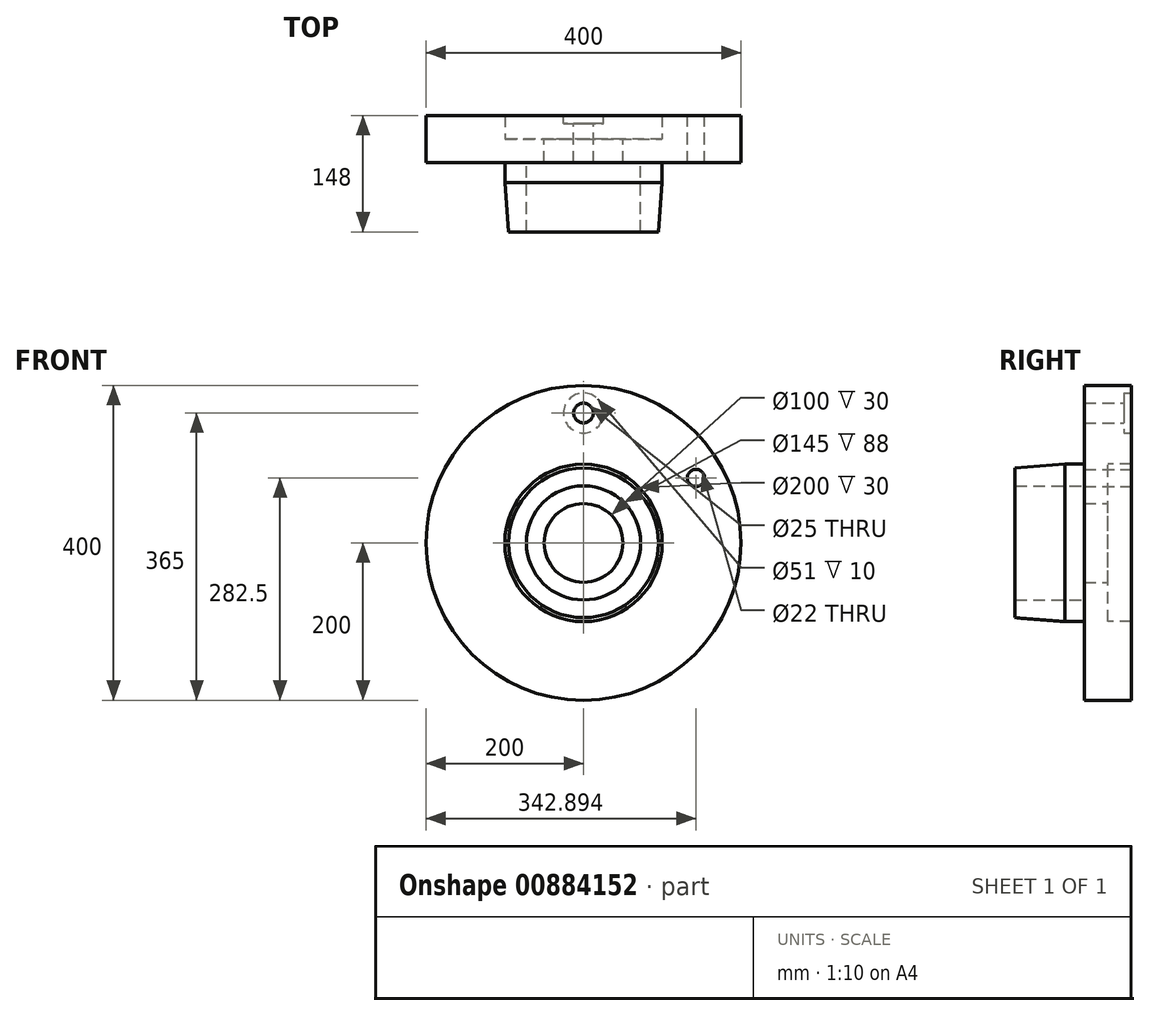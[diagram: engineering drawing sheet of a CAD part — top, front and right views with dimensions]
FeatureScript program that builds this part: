
annotation { "Feature Type Name" : "Feature", "Feature Type Description" : "" }
export const myFeature = defineFeature(function(context is Context, id is Id, definition is map)
    precondition{}
    {
        {
            var Q0;
            Q0=qCreatedBy(makeId("Front.planeOp"),FACE);
            var sketch = newSketch(context, id + "F0", { "sketchPlane" : qUnion([Q0])});
            skCircle(sketch, "E0", {"center": v(0, 0) * mm, "radius": 72.5 * mm});
            skCircle(sketch, "E1", {"center": v(0, 0) * mm, "radius": 100 * mm});
            skCircle(sketch, "E2", {"center": v(0, 0) * mm, "radius": 50 * mm});
            skCircle(sketch, "E3", {"center": v(0, 0) * mm, "radius": 200 * mm});
            skCircle(sketch, "E4", {"center": v(0, 0) * mm, "radius": 165 * mm, "construction": true});
            skPoint(sketch, "E5", {"position": v(0, 165) * mm});
            skLineSegment(sketch, "E6", {"start": v(0, 0) * mm, "end": v(142.9, 82.5) * mm, "construction": true});
            skPoint(sketch, "E7", {"position": v(142.9, 82.5) * mm});
            skSolve(sketch);
        }
        {
            var Q0;
            Q0=makeQuery(id+"F0.imprint","IMPRINT",FACE,{"disambiguationData":[TD([[makeQuery(id+"F0.imprint","IMPRINT",EDGE,{"derivedFrom":sQuery(id+"F0.wireOp",EDGE,"E0")}),-1.0]])]});
            var Q1;
            Q1=makeQuery(id+"F0.imprint","IMPRINT",FACE,{"disambiguationData":[TD([[makeQuery(id+"F0.imprint","IMPRINT",EDGE,{"derivedFrom":sQuery(id+"F0.wireOp",EDGE,"E0")}),1.0]])]});
            var Q2;
            Q2=makeQuery(id+"F0.imprint","IMPRINT",FACE,{"disambiguationData":[TD([[makeQuery(id+"F0.imprint","IMPRINT",EDGE,{"derivedFrom":sQuery(id+"F0.wireOp",EDGE,"E1")}),-1.0]])]});
            extrude(context, id + "F1", {"entities" : qUnion([Q0, Q1, Q2]), "depth" : 30 * mm, "offsetDistance" : 25 * mm});
        }
        {
            var Q0;
            Q0=makeQuery(id+"F0.imprint","IMPRINT",FACE,{"disambiguationData":[TD([[makeQuery(id+"F0.imprint","IMPRINT",EDGE,{"derivedFrom":sQuery(id+"F0.wireOp",EDGE,"E0")}),-1.0]])]});
            extrude(context, id + "F2", {"entities" : qUnion([Q0]), "operationType" : NewBodyOperationType.ADD, "depth" : (70 + 48) * mm, "offsetDistance" : 25 * mm});
        }
        {
            var Q0;
            Q0=makeQuery(id+"F0.imprint","IMPRINT",FACE,{"disambiguationData":[TD([[makeQuery(id+"F0.imprint","IMPRINT",EDGE,{"derivedFrom":sQuery(id+"F0.wireOp",EDGE,"E1")}),-1.0]])]});
            extrude(context, id + "F3", {"entities" : qUnion([Q0]), "operationType" : NewBodyOperationType.ADD, "oppositeDirection" : true, "depth" : 30 * mm, "offsetDistance" : 25 * mm});
        }
        {
            var Q0;
            Q0=makeQuery(id+"F3.opExtrude","CAP_FACE",FACE,{"disambiguationData":[OSD([sQuery(id+"F0.wireOp",EDGE,"E1"),sQuery(id+"F0.wireOp",EDGE,"E3")])],"isStart":false});
            var sketch = newSketch(context, id + "F4", { "sketchPlane" : qUnion([Q0])});
            skCircle(sketch, "E8.0", {"center": v(0, 0) * mm, "radius": 165 * mm});
            skPoint(sketch, "E9.0", {"position": v(0, 165) * mm});
            skPoint(sketch, "E10.0", {"position": v(-142.9, 82.5) * mm});
            skSolve(sketch);
        }
        {
            var Q0;
            Q0=sQuery(id+"F4.wireOp",VERTEX,"E9.0");
            var Q1;
            Q1=makeQuery(id+"F1.opExtrude","SWEPT_BODY",BODY,{"disambiguationData":[OSD([sQuery(id+"F0.wireOp",EDGE,"E2"),sQuery(id+"F0.wireOp",EDGE,"E3")])]});
            hole(context, id + "F5", {"style" : HoleStyle.C_BORE, "endStyle" : HoleEndStyle.THROUGH, "holeDiameter" : 25 * mm, "cBoreDiameter" : 51 * mm, "cBoreDepth" : 10 * mm, "majorDiameter" : 5 * mm, "isTappedThrough" : true, "tappedDepth" : 12 * mm, "tapClearance" : 3, "locations" : qUnion([Q0]), "scope" : qUnion([Q1])});
        }
        {
            var Q0;
            Q0=sQuery(id+"F4.wireOp",VERTEX,"E10.0");
            var Q1;
            Q1=makeQuery(id+"F1.opExtrude","SWEPT_BODY",BODY,{"disambiguationData":[OSD([sQuery(id+"F0.wireOp",EDGE,"E2"),sQuery(id+"F0.wireOp",EDGE,"E3")])]});
            hole(context, id + "F6", {"style" : HoleStyle.SIMPLE, "endStyle" : HoleEndStyle.THROUGH, "standardTappedOrClearance" : lookupTablePath({ "fit" : "Normal", "standard" : "ISO", "size" : "M20", "type" : "Clearance" }), "standardBlindInLast" : lookupTablePath({ "fit" : "Normal", "standard" : "ISO", "size" : "M20", "type" : "Clearance" }), "holeDiameter" : 22 * mm, "majorDiameter" : 5 * mm, "isTappedThrough" : true, "tappedDepth" : 12 * mm, "tapClearance" : 3, "locations" : qUnion([Q0]), "scope" : qUnion([Q1])});
        }
        {
            var Q0;
            Q0=makeQuery(id+"F2.opExtrude","CAP_EDGE",EDGE,{"disambiguationData":[OSD([sQuery(id+"F0.wireOp",EDGE,"E1")])],"isStart":false});
            chamfer(context, id + "F7", {"entities" : qUnion([Q0]), "chamferType" : ChamferType.TWO_OFFSETS, "width1" : 5 * mm, "oppositeDirection" : false, "width2" : 63 * mm, "tangentPropagation" : true});
        }
    });
